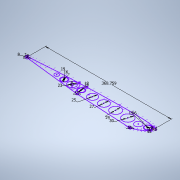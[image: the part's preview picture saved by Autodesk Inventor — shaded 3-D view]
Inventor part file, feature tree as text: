
AUTODESK INVENTOR PART (.ipt)
format: ipt  version: 2022 (Build 260153000, 153)  size: 206,848 bytes
history: native  units: mm
features: sketch x1
ambient origin geometry x8: Origin, YZ Plane, XZ Plane, XY Plane, X Axis, Y Axis, Z Axis, Center Point
feature tree (1):
  sketch  "Sketch1"  dims[d31=34.456mm d50=368.759386mm d57=16.0mm d69=8.0mm d70=23.0mm d71=8.0mm d73=16.0mm d80=19.0mm d81=16.0mm d82=1.0mm d83=1.0mm d84=1.0mm d85=1.0mm d86=1.0mm d87=0.8mm d88=1.0mm d90=19.0mm d94=5.0mm d95=5.0mm d101=5.0mm d102=5.0mm d105=5.0mm d106=5.0mm d108=2.0mm d109=19.0mm d110=30.0mm d111=29.0mm d112=27.0mm d113=25.0mm]
